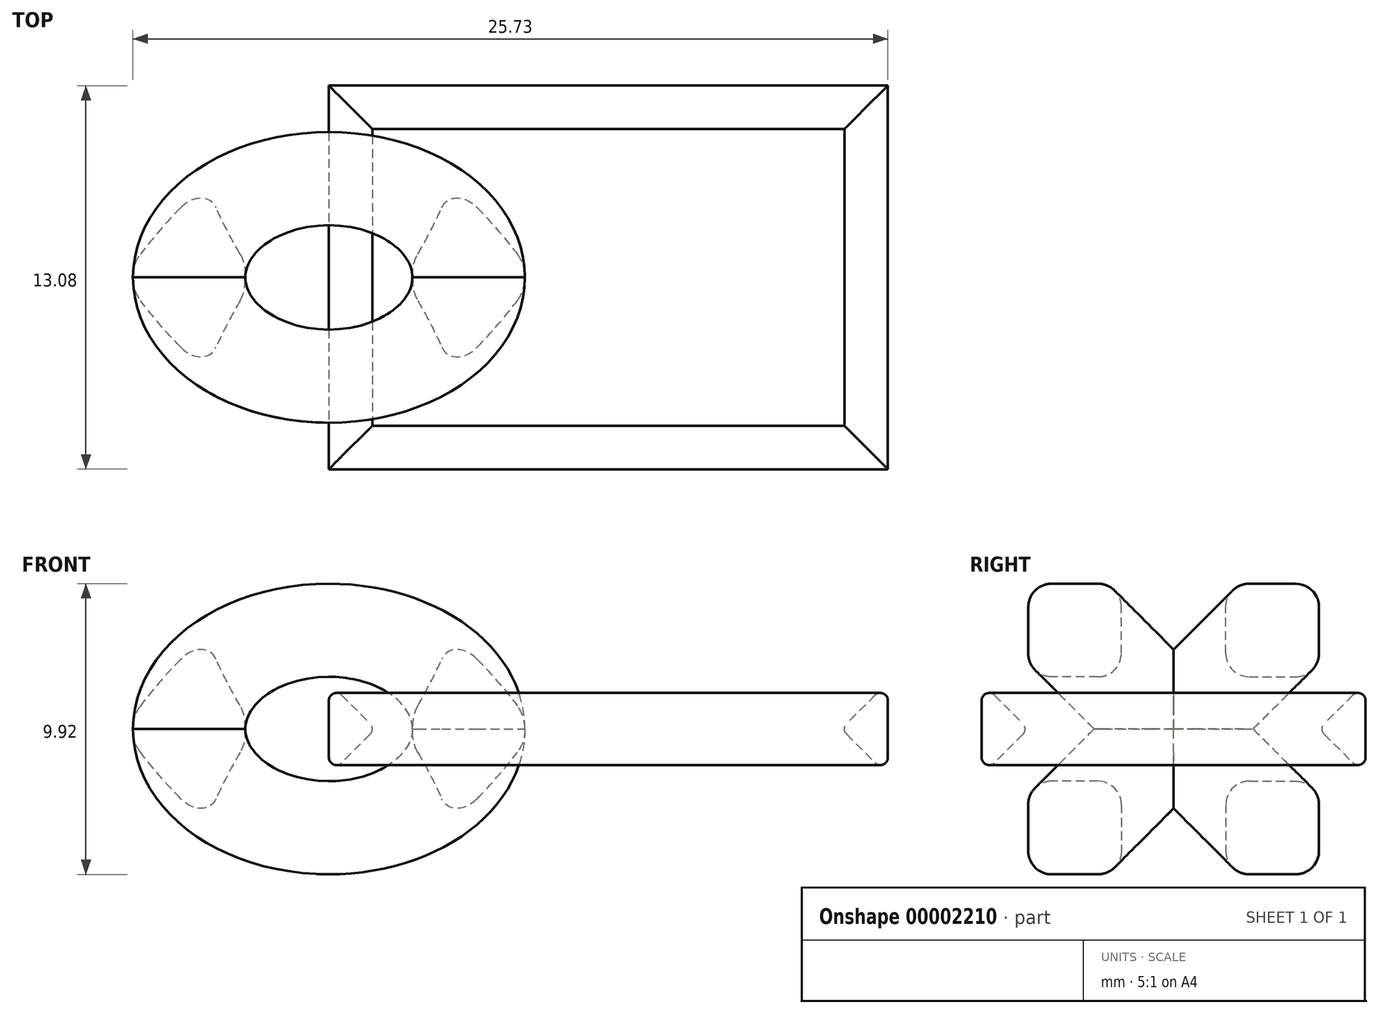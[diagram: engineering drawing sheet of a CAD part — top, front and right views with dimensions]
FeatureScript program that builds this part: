
annotation { "Feature Type Name" : "Feature", "Feature Type Description" : "" }
export const myFeature = defineFeature(function(context is Context, id is Id, definition is map)
    precondition{}
    {
        {
            var Q0;
            Q0=qCreatedBy(makeId("Top.planeOp"),FACE);
            var sketch = newSketch(context, id + "F0", { "sketchPlane" : qUnion([Q0])});
            skLineSegment(sketch, "E0", {"start": v(0, 0) * mm, "end": v(75, 0) * mm, "construction": true});
            skSolve(sketch);
        }
        {
            var Q0;
            Q0=sQuery(id+"F0.wireOp",EDGE,"E0");
            cPlane(context, id + "F1", {"entities" : qUnion([Q0]), "cplaneType" : CPlaneType.LINE_ANGLE, "offset" : 152.4 * mm, "angle" : 45 * degree, "width" : 152.4 * mm, "height" : 152.4 * mm});
        }
        {
            var Q0;
            Q0=sQuery(id+"F0.wireOp",EDGE,"E0");
            cPlane(context, id + "F2", {"entities" : qUnion([Q0]), "cplaneType" : CPlaneType.LINE_ANGLE, "offset" : 152.4 * mm, "angle" : 315 * degree, "width" : 152.4 * mm, "height" : 152.4 * mm});
        }
        {
            var Q0;
            Q0=qCreatedBy(id+"F2.planeOp",FACE);
            var sketch = newSketch(context, id + "F3", { "sketchPlane" : qUnion([Q0])});
            skCircle(sketch, "E1", {"center": v(0, 0) * mm, "radius": 4.76 * mm});
            skSolve(sketch);
        }
        {
            var Q0;
            Q0=qCreatedBy(id+"F1.planeOp",FACE);
            var sketch = newSketch(context, id + "F4", { "sketchPlane" : qUnion([Q0])});
            skCircle(sketch, "E2", {"center": v(0, 0) * mm, "radius": 4.76 * mm});
            skSolve(sketch);
        }
        {
            var Q0;
            Q0=qCreatedBy(id+"F1.planeOp",FACE);
            var sketch = newSketch(context, id + "F5", { "sketchPlane" : qUnion([Q0])});
            skLineSegment(sketch, "E3.0", {"start": v(4.76, 0) * mm, "end": v(-4.76, 0) * mm});
            skLineSegment(sketch, "E4", {"start": v(-3.08, 0.56) * mm, "end": v(-4.2, 1.68) * mm});
            skLineSegment(sketch, "E5", {"start": v(-5.32, 1.68) * mm, "end": v(-6.45, 0.56) * mm});
            skLineSegment(sketch, "E6", {"start": v(-6.45, -0.56) * mm, "end": v(-5.32, -1.68) * mm});
            skLineSegment(sketch, "E7", {"start": v(-4.2, -1.68) * mm, "end": v(-3.08, -0.56) * mm});
            skPoint(sketch, "E8.visualSharp", {"position": v(-7, 0) * mm});
            skArc(sketch, "E8.filletArc", {"start": v(-6.45, 0.56) * mm, "mid": v(-6.68, 0) * mm, "end": v(-6.45, -0.56) * mm});
            skPoint(sketch, "E9.visualSharp", {"position": v(-4.76, -2.25) * mm});
            skArc(sketch, "E9.filletArc", {"start": v(-5.32, -1.68) * mm, "mid": v(-4.76, -1.92) * mm, "end": v(-4.2, -1.68) * mm});
            skPoint(sketch, "E10.visualSharp", {"position": v(-2.52, 0) * mm});
            skArc(sketch, "E10.filletArc", {"start": v(-3.08, -0.56) * mm, "mid": v(-2.85, 0) * mm, "end": v(-3.08, 0.56) * mm});
            skPoint(sketch, "E11.visualSharp", {"position": v(-4.76, 2.25) * mm});
            skArc(sketch, "E11.filletArc", {"start": v(-4.2, 1.68) * mm, "mid": v(-4.76, 1.92) * mm, "end": v(-5.32, 1.68) * mm});
            skSolve(sketch);
        }
        {
            var Q0;
            {var subQ3=sQuery(id+"F5.wireOp",EDGE,"E4");Q0=makeQuery(id+"F5.imprint","IMPRINT",FACE,{"disambiguationData":[TD([[makeQuery(id+"F5.imprint","IMPRINT",EDGE,{"derivedFrom":subQ3}),1.0]])]});}
            var Q1;
            Q1=sQuery(id+"F3.wireOp",EDGE,"E1");
            sweep(context, id + "F6", {"profiles" : qUnion([Q0]), "path" : qUnion([Q1])});
        }
        {
            var Q0;
            Q0=qCreatedBy(id+"F2.planeOp",FACE);
            var sketch = newSketch(context, id + "F7", { "sketchPlane" : qUnion([Q0])});
            skLineSegment(sketch, "E12.0", {"start": v(4.76, 0) * mm, "end": v(-4.76, 0) * mm});
            skLineSegment(sketch, "E13", {"start": v(3.08, 0.56) * mm, "end": v(4.2, 1.68) * mm});
            skLineSegment(sketch, "E14", {"start": v(5.32, 1.68) * mm, "end": v(6.45, 0.56) * mm});
            skLineSegment(sketch, "E15", {"start": v(6.45, -0.56) * mm, "end": v(5.32, -1.68) * mm});
            skLineSegment(sketch, "E16", {"start": v(4.2, -1.68) * mm, "end": v(3.08, -0.56) * mm});
            skPoint(sketch, "E17.visualSharp", {"position": v(7, 0) * mm});
            skArc(sketch, "E17.filletArc", {"start": v(6.45, -0.56) * mm, "mid": v(6.68, 0) * mm, "end": v(6.45, 0.56) * mm});
            skPoint(sketch, "E18.visualSharp", {"position": v(4.76, -2.25) * mm});
            skArc(sketch, "E18.filletArc", {"start": v(4.2, -1.68) * mm, "mid": v(4.76, -1.92) * mm, "end": v(5.32, -1.68) * mm});
            skPoint(sketch, "E19.visualSharp", {"position": v(2.52, 0) * mm});
            skArc(sketch, "E19.filletArc", {"start": v(3.08, 0.56) * mm, "mid": v(2.85, 0) * mm, "end": v(3.08, -0.56) * mm});
            skPoint(sketch, "E20.visualSharp", {"position": v(4.76, 2.25) * mm});
            skArc(sketch, "E20.filletArc", {"start": v(5.32, 1.68) * mm, "mid": v(4.76, 1.92) * mm, "end": v(4.2, 1.68) * mm});
            skSolve(sketch);
        }
        {
            var Q0;
            {var subQ4=sQuery(id+"F7.wireOp",EDGE,"E13");Q0=makeQuery(id+"F7.imprint","IMPRINT",FACE,{"disambiguationData":[TD([[makeQuery(id+"F7.imprint","IMPRINT",EDGE,{"derivedFrom":subQ4}),-1.0]])]});}
            var Q1;
            Q1=sQuery(id+"F4.wireOp",EDGE,"E2");
            sweep(context, id + "F8", {"profiles" : qUnion([Q0]), "path" : qUnion([Q1])});
        }
        {
            var Q0;
            Q0=makeQuery(id+"F6.opSweep","SWEPT_BODY",BODY,{"disambiguationData":[OSD([sQuery(id+"F3.wireOp",EDGE,"E1"),sQuery(id+"F5.wireOp",EDGE,"E4"),sQuery(id+"F5.wireOp",EDGE,"E5"),sQuery(id+"F5.wireOp",EDGE,"E6"),sQuery(id+"F5.wireOp",EDGE,"E7"),sQuery(id+"F5.wireOp",EDGE,"E8.filletArc"),sQuery(id+"F5.wireOp",EDGE,"E9.filletArc"),sQuery(id+"F5.wireOp",EDGE,"E10.filletArc"),sQuery(id+"F5.wireOp",EDGE,"E11.filletArc")])]});
            var Q1;
            Q1=makeQuery(id+"F8.opSweep","SWEPT_BODY",BODY,{"disambiguationData":[OSD([sQuery(id+"F4.wireOp",EDGE,"E2"),sQuery(id+"F7.wireOp",EDGE,"E13"),sQuery(id+"F7.wireOp",EDGE,"E14"),sQuery(id+"F7.wireOp",EDGE,"E15"),sQuery(id+"F7.wireOp",EDGE,"E16"),sQuery(id+"F7.wireOp",EDGE,"E17.filletArc"),sQuery(id+"F7.wireOp",EDGE,"E18.filletArc"),sQuery(id+"F7.wireOp",EDGE,"E19.filletArc"),sQuery(id+"F7.wireOp",EDGE,"E20.filletArc")])]});
            booleanBodies(context, id + "F9", {"operationType" : BooleanOperationType.UNION, "tools" : qUnion([Q0, Q1])});
        }
        {
            var Q0;
            Q0=qCreatedBy(makeId("Top.planeOp"),FACE);
            var sketch = newSketch(context, id + "F10", { "sketchPlane" : qUnion([Q0])});
            skPoint(sketch, "E21.0", {"position": v(0, 0) * mm});
            skLineSegment(sketch, "E22.rect.bottom", {"start": v(0, -6.54) * mm, "end": v(19.05, -6.54) * mm});
            skLineSegment(sketch, "E22.rect.top", {"start": v(0, 6.54) * mm, "end": v(19.05, 6.54) * mm});
            skLineSegment(sketch, "E22.rect.left", {"start": v(0, -6.54) * mm, "end": v(0, 6.54) * mm});
            skLineSegment(sketch, "E22.rect.right", {"start": v(19.05, -6.54) * mm, "end": v(19.05, 6.54) * mm});
            skPoint(sketch, "E22.rect.middle", {"position": v(9.53, 0) * mm});
            skPoint(sketch, "E23.visualSharp", {"position": v(0, -6.54) * mm});
            skPoint(sketch, "E24.visualSharp", {"position": v(19.05, -6.54) * mm});
            skPoint(sketch, "E25.visualSharp", {"position": v(19.05, 6.54) * mm});
            skPoint(sketch, "E26.visualSharp", {"position": v(0, 6.54) * mm});
            skSolve(sketch);
        }
        {
            var Q0;
            Q0=qCreatedBy(makeId("Right.planeOp"),FACE);
            var sketch = newSketch(context, id + "F11", { "sketchPlane" : qUnion([Q0])});
            skLineSegment(sketch, "E27.0", {"start": v(-4.16, 1.78) * mm, "end": v(-2.38, 0) * mm});
            skLineSegment(sketch, "E28.0.2", {"start": v(-2.38, 0) * mm, "end": v(-4.16, -1.78) * mm});
            skLineSegment(sketch, "E29.0.1", {"start": v(-4.96, 2.57) * mm, "end": v(-2.38, 0) * mm});
            skFitSpline(sketch, "E30.0.0", {"points": [v(-2.38, 0) * mm, v(-1.85, 0) * mm, v(-1.32, 0) * mm, v(-0.8, 0) * mm]});
            skFitSpline(sketch, "E30.0.2", {"points": [v(-0.8, 0) * mm, v(-1.32, 0) * mm, v(-1.85, 0) * mm, v(-2.38, 0) * mm]});
            skLineSegment(sketch, "E30.0.3", {"start": v(-4.96, 4.16) * mm, "end": v(-0.8, 0) * mm});
            skLineSegment(sketch, "E31", {"start": v(-4.96, 0) * mm, "end": v(-6.54, -1.59) * mm});
            skLineSegment(sketch, "E32", {"start": v(-6.54, -1.59) * mm, "end": v(-6.54, 1.59) * mm});
            skLineSegment(sketch, "E33", {"start": v(-6.54, 1.59) * mm, "end": v(-4.96, 0) * mm});
            skLineSegment(sketch, "E34.0.0", {"start": v(-2.38, 0) * mm, "end": v(-4.96, -2.57) * mm});
            skFitSpline(sketch, "E34.0.1", {"points": [v(-2.38, 0) * mm, v(-1.85, 0) * mm, v(-1.32, 0) * mm, v(-0.8, 0) * mm]});
            skLineSegment(sketch, "E34.0.2", {"start": v(-0.8, 0) * mm, "end": v(-4.96, -4.16) * mm});
            skFitSpline(sketch, "E34.0.3", {"points": [v(-0.8, 0) * mm, v(-1.32, 0) * mm, v(-1.85, 0) * mm, v(-2.38, 0) * mm]});
            skSolve(sketch);
        }
        {
            var Q0;
            Q0=makeQuery(id+"F11.imprint","IMPRINT",FACE,{"disambiguationData":[TD([[makeQuery(id+"F11.imprint","IMPRINT",EDGE,{"derivedFrom":sQuery(id+"F11.wireOp",EDGE,"E31")}),-1.0]])]});
            var Q1;
            Q1=sQuery(id+"F10.wireOp",EDGE,"E22.rect.bottom");
            var Q2;
            Q2=sQuery(id+"F10.wireOp",EDGE,"E22.rect.right");
            var Q3;
            Q3=sQuery(id+"F10.wireOp",EDGE,"E22.rect.top");
            var Q4;
            Q4=sQuery(id+"F10.wireOp",EDGE,"E22.rect.left");
            sweep(context, id + "F12", {"profiles" : qUnion([Q0]), "path" : qUnion([Q1, Q2, Q3, Q4])});
        }
        {
            var Q0;
            Q0=makeQuery(id+"F12.opSweep","SWEPT_EDGE",EDGE,{"disambiguationData":[OSD([sQuery(id+"F10.wireOp",EDGE,"E22.rect.right"),sQuery(id+"F11.wireOp",EDGE,"E31"),sQuery(id+"F11.wireOp",EDGE,"E32")])]});
            var Q1;
            Q1=makeQuery(id+"F12.opSweep","SWEPT_EDGE",EDGE,{"disambiguationData":[OSD([sQuery(id+"F10.wireOp",EDGE,"E22.rect.bottom"),sQuery(id+"F11.wireOp",EDGE,"E31"),sQuery(id+"F11.wireOp",EDGE,"E32")])]});
            var Q2;
            Q2=makeQuery(id+"F12.opSweep","SWEPT_EDGE",EDGE,{"disambiguationData":[OSD([sQuery(id+"F10.wireOp",EDGE,"E22.rect.top"),sQuery(id+"F11.wireOp",EDGE,"E31"),sQuery(id+"F11.wireOp",EDGE,"E32")])]});
            var Q3;
            Q3=makeQuery(id+"F12.opSweep","SWEPT_EDGE",EDGE,{"disambiguationData":[OSD([sQuery(id+"F10.wireOp",EDGE,"E22.rect.left"),sQuery(id+"F11.wireOp",EDGE,"E31"),sQuery(id+"F11.wireOp",EDGE,"E32")])]});
            var Q4;
            Q4=makeQuery(id+"F12.opSweep","SWEPT_EDGE",EDGE,{"disambiguationData":[OSD([sQuery(id+"F10.wireOp",EDGE,"E22.rect.top"),sQuery(id+"F11.wireOp",EDGE,"E31"),sQuery(id+"F11.wireOp",EDGE,"E33")])]});
            var Q5;
            Q5=makeQuery(id+"F12.opSweep","SWEPT_EDGE",EDGE,{"disambiguationData":[OSD([sQuery(id+"F10.wireOp",EDGE,"E22.rect.right"),sQuery(id+"F11.wireOp",EDGE,"E31"),sQuery(id+"F11.wireOp",EDGE,"E33")])]});
            var Q6;
            Q6=makeQuery(id+"F12.opSweep","SWEPT_EDGE",EDGE,{"disambiguationData":[OSD([sQuery(id+"F10.wireOp",EDGE,"E22.rect.bottom"),sQuery(id+"F11.wireOp",EDGE,"E31"),sQuery(id+"F11.wireOp",EDGE,"E33")])]});
            var Q7;
            Q7=makeQuery(id+"F12.opSweep","SWEPT_EDGE",EDGE,{"disambiguationData":[OSD([sQuery(id+"F10.wireOp",EDGE,"E22.rect.left"),sQuery(id+"F11.wireOp",EDGE,"E31"),sQuery(id+"F11.wireOp",EDGE,"E33")])]});
            var Q8;
            Q8=makeQuery(id+"F12.opSweep","SWEPT_EDGE",EDGE,{"disambiguationData":[OSD([sQuery(id+"F10.wireOp",EDGE,"E22.rect.right"),sQuery(id+"F11.wireOp",EDGE,"E32"),sQuery(id+"F11.wireOp",EDGE,"E33")])]});
            var Q9;
            Q9=makeQuery(id+"F12.opSweep","SWEPT_EDGE",EDGE,{"disambiguationData":[OSD([sQuery(id+"F10.wireOp",EDGE,"E22.rect.bottom"),sQuery(id+"F11.wireOp",EDGE,"E32"),sQuery(id+"F11.wireOp",EDGE,"E33")])]});
            var Q10;
            Q10=makeQuery(id+"F12.opSweep","SWEPT_EDGE",EDGE,{"disambiguationData":[OSD([sQuery(id+"F10.wireOp",EDGE,"E22.rect.top"),sQuery(id+"F11.wireOp",EDGE,"E32"),sQuery(id+"F11.wireOp",EDGE,"E33")])]});
            var Q11;
            Q11=makeQuery(id+"F12.opSweep","SWEPT_EDGE",EDGE,{"disambiguationData":[OSD([sQuery(id+"F10.wireOp",EDGE,"E22.rect.left"),sQuery(id+"F11.wireOp",EDGE,"E32"),sQuery(id+"F11.wireOp",EDGE,"E33")])]});
            fillet(context, id + "F13", {"entities" : qUnion([Q0, Q1, Q2, Q3, Q4, Q5, Q6, Q7, Q8, Q9, Q10, Q11]), "radius" : 0.25 * mm, "tangentPropagation" : true, "allowEdgeOverflow" : false});
        }
    });
